# Revit family: Rio 2700K
name_source: partatom
category: Lighting Fixtures
revit_build: Autodesk Revit 2018 (Build: 20170223_1515(x64)
units: mm (PartAtom-declared; Revit-internal decimal feet)

## family parameters
Cut with Voids When Loaded = No
Host = Face
Light Source = Yes
OmniClass Number = 23.80.70.00
OmniClass Title = Lighting
Part Type = Normal
Room Calculation Point = No
Round Connector Dimension = Use Diameter
Shared = No

## types (2) — shared parameters
Apparent Load = 17 VA
Assembly Code = D5020200
Casing Material = Astro - Plaster - Natural
Class = 1
Color Filter = 16777215
Description = Wall light
Dimming Lamp Color Temperature Shift = <None>
Emit Shape Visible in Rendering = No
IP Rating = IP20
Lamp = LED
Lamp included = Yes
Length = 55 mm  [stored 0.180446 ft]
Light Source Elevation = 1600 mm  [stored 5.24934 ft]
Light Source From Wall = 30 mm  [stored 0.0984252 ft]
Luminaire Lamp Efficiency Rating = A
Manufacturer = Astro Lighting Ltd, CM20 2DP
Mountable on normally flammable surfaces = Yes
Number of Poles = 1
Product Documentation = http://www.astrolighting.co.uk
/kw/7173/7173_Rio-190
/kw/RIO/7172_Rio-325
Suitable for bathroom zone = Zone 3
Tilt Angle = 90.00°
Type Comments = Includes integrated 1-10v dimmable driver
URL = www.astrolighting.co.uk
Voltage = 230 V
Wall Bracket Material = Astro - Aluminium - Anodised
Weight = 2.75 kg

## per-type parameters (varying)
| type | Cable Entry Placer (from bottom) | Cable Entry Placer (from right) | Diffuser Length | Diffuser Width | Dimmable | Emit from Rectangle Length | Emit from Rectangle Width | Height | Model | Photometric Web File | Wall Bracket Height | Wattage Comments | Width |
| Rio 325 2700K (CE) | 90 mm | 80.5 mm | 25 mm  [stored 0.082021 ft] | 304 mm  [stored 0.997375 ft] | See datasheet | 25 mm  [stored 0.082021 ft] | 304 mm  [stored 0.997375 ft] | 180 mm  [stored 0.590551 ft] | 7172 Rio 325 | GNC-19600  8053 - Rio 325 LED 2700K Phase Dimmable  ies.ies | 80 mm | 16.4 | 325 mm  [stored 1.06627 ft] |
| Rio 190 2700K (CE) | 91 mm  [stored 0.298556 ft] | 95 mm | 22 mm  [stored 0.0721785 ft] | 168 mm  [stored 0.551181 ft] | See Datasheet | 22 mm  [stored 0.0721785 ft] | 168 mm  [stored 0.551181 ft] | 325 mm  [stored 1.06627 ft] | 7173 Rio 190 | GNC-19601  8054 - Rio 190 LED 2700K Phase Dimmable ies.ies | 224 mm  [stored 0.734908 ft] | 16.6 | 190 mm |

note: [stored X ft] marks values corroborated as IEEE doubles in the binary element streams (Revit-internal decimal feet)

## geometry (parser evidence)
native form markers: Sweep x3
no freeform markers — native parametric forms only
